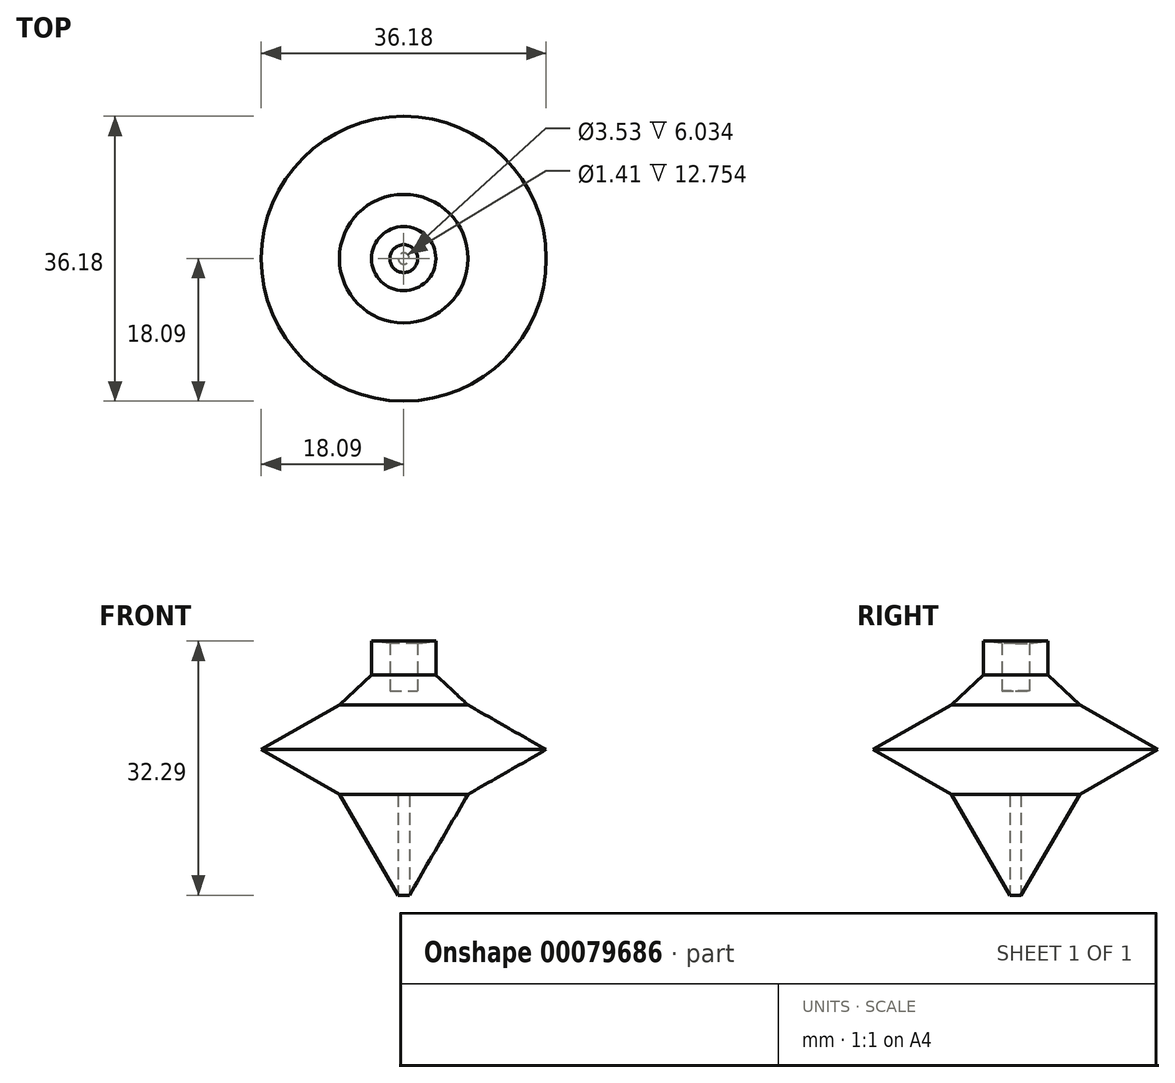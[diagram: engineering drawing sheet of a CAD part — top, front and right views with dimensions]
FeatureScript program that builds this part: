
annotation { "Feature Type Name" : "Feature", "Feature Type Description" : "" }
export const myFeature = defineFeature(function(context is Context, id is Id, definition is map)
    precondition{}
    {
        {
            var Q0;
            Q0=qCreatedBy(makeId("Front.planeOp"),FACE);
            var sketch = newSketch(context, id + "F0", { "sketchPlane" : qUnion([Q0])});
            skLineSegment(sketch, "E0", {"start": v(0, 0) * mm, "end": v(8.17, 14.06) * mm});
            skLineSegment(sketch, "E1", {"start": v(18.1, 19.72) * mm, "end": v(8.17, 14.06) * mm});
            skLineSegment(sketch, "E2", {"start": v(18.1, 19.72) * mm, "end": v(8.17, 25.4) * mm});
            skLineSegment(sketch, "E3", {"start": v(8.17, 25.4) * mm, "end": v(0, 33.02) * mm});
            skLineSegment(sketch, "E4", {"start": v(0, 33.02) * mm, "end": v(0, 0) * mm});
            skLineSegment(sketch, "E5", {"start": v(4.08, 29.2) * mm, "end": v(4.08, 33.51) * mm});
            skLineSegment(sketch, "E6", {"start": v(4.08, 33.51) * mm, "end": v(0, 33.02) * mm});
            skSolve(sketch);
        }
        {
            var Q0;
            Q0=makeQuery(id+"F0.imprint","IMPRINT",FACE,{"disambiguationData":[TD([[makeQuery(id+"F0.imprint","IMPRINT",EDGE,{"derivedFrom":sQuery(id+"F0.wireOp",EDGE,"E0")}),1.0]])]});
            var Q1;
            {var subQ2=sQuery(id+"F0.wireOp",EDGE,"E5");Q1=makeQuery(id+"F0.imprint","IMPRINT",FACE,{"disambiguationData":[TD([[makeQuery(id+"F0.imprint","IMPRINT",EDGE,{"derivedFrom":subQ2}),1.0]])]});}
            var Q2;
            Q2=sQuery(id+"F0.wireOp",EDGE,"E4");
            revolve(context, id + "F1", {"entities" : qUnion([Q0, Q1]), "axis" : qUnion([Q2]), "revolveType" : RevolveType.FULL});
        }
        {
            var Q0;
            Q0=qCreatedBy(makeId("Front.planeOp"),FACE);
            var sketch = newSketch(context, id + "F2", { "sketchPlane" : qUnion([Q0])});
            skLineSegment(sketch, "E7", {"start": v(0, 33.55) * mm, "end": v(1.77, 33.55) * mm});
            skLineSegment(sketch, "E8", {"start": v(1.77, 33.55) * mm, "end": v(1.77, 29.2) * mm});
            skLineSegment(sketch, "E9", {"start": v(1.77, 29.2) * mm, "end": v(0, 29.2) * mm});
            skLineSegment(sketch, "E10", {"start": v(0, 29.2) * mm, "end": v(0, 33.55) * mm});
            skSolve(sketch);
        }
        {
            var Q0;
            Q0 = qSketchRegion(id + "F2", true);
            var Q1;
            Q1=sQuery(id+"F2.wireOp",EDGE,"E10");
            revolve(context, id + "F3", {"operationType" : NewBodyOperationType.ADD, "entities" : qUnion([Q0]), "axis" : qUnion([Q1]), "revolveType" : RevolveType.FULL});
        }
        {
            var Q0;
            Q0=makeQuery(id+"F3.opRevolve","SWEPT_FACE",FACE,{"disambiguationData":[OSD([sQuery(id+"F2.wireOp",EDGE,"E7")])]});
            extrude(context, id + "F4", {"entities" : qUnion([Q0]), "operationType" : NewBodyOperationType.REMOVE, "endBound" : BoundingType.SYMMETRIC, "depth" : 12.7 * mm});
        }
        {
            var Q0;
            Q0=qCreatedBy(makeId("Front.planeOp"),FACE);
            var sketch = newSketch(context, id + "F5", { "sketchPlane" : qUnion([Q0])});
            skLineSegment(sketch, "E11", {"start": v(0.7, 0) * mm, "end": v(0.7, 3.59) * mm});
            skLineSegment(sketch, "E12", {"start": v(0.7, 3.59) * mm, "end": v(0, 3.59) * mm});
            skLineSegment(sketch, "E13", {"start": v(0, 3.59) * mm, "end": v(0, 0) * mm});
            skLineSegment(sketch, "E14", {"start": v(0, 0) * mm, "end": v(0.7, 0) * mm});
            skSolve(sketch);
        }
        {
            var Q0;
            Q0 = qSketchRegion(id + "F5", true);
            var Q1;
            Q1=sQuery(id+"F5.wireOp",EDGE,"E13");
            revolve(context, id + "F6", {"operationType" : NewBodyOperationType.ADD, "entities" : qUnion([Q0]), "axis" : qUnion([Q1]), "revolveType" : RevolveType.FULL});
        }
        {
            var Q0;
            Q0=makeQuery(id+"F6.opRevolve","SWEPT_FACE",FACE,{"disambiguationData":[OSD([sQuery(id+"F5.wireOp",EDGE,"E14")])]});
            extrude(context, id + "F7", {"entities" : qUnion([Q0]), "operationType" : NewBodyOperationType.REMOVE, "oppositeDirection" : true, "depth" : 13.97 * mm});
        }
    });
